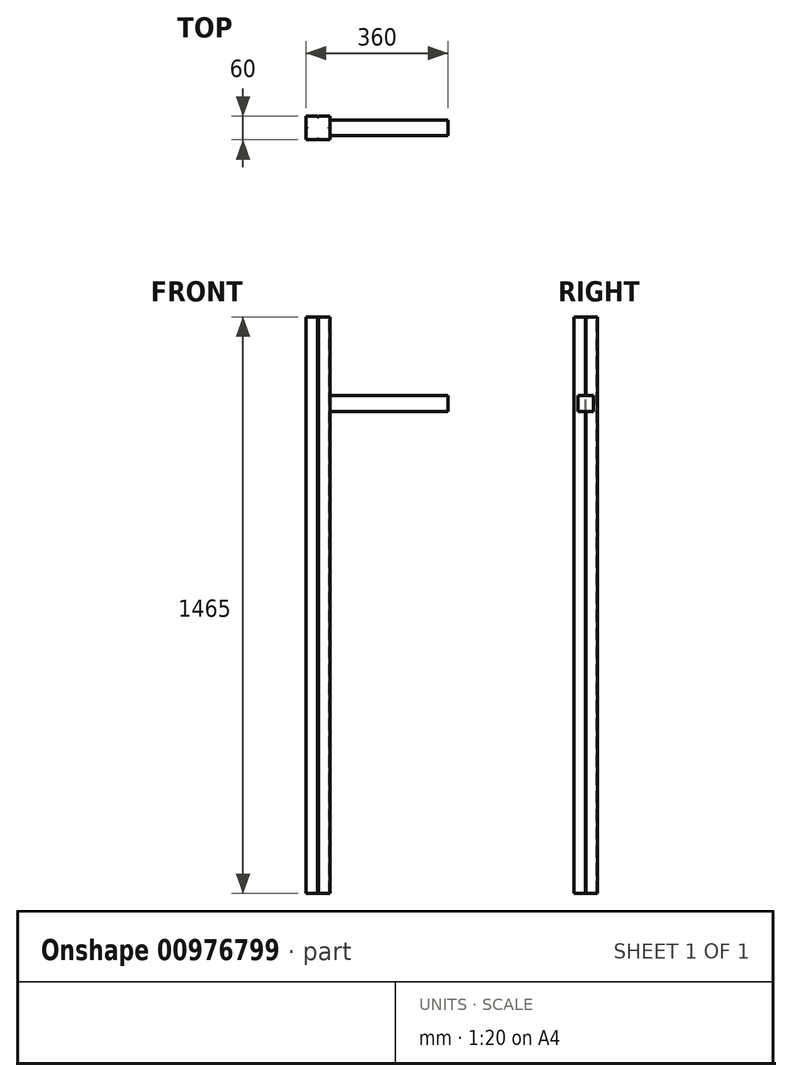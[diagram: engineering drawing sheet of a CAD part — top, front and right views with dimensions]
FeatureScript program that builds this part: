
annotation { "Feature Type Name" : "Feature", "Feature Type Description" : "" }
export const myFeature = defineFeature(function(context is Context, id is Id, definition is map)
    precondition{}
    {
        {
            var Q0;
            Q0=qCreatedBy(makeId("Top.planeOp"),FACE);
            var sketch = newSketch(context, id + "F0", { "sketchPlane" : qUnion([Q0])});
            skLineSegment(sketch, "E0.bottom", {"start": v(30, -30) * mm, "end": v(-30, -30) * mm});
            skLineSegment(sketch, "E0.top", {"start": v(30, 30) * mm, "end": v(-30, 30) * mm});
            skLineSegment(sketch, "E0.left", {"start": v(30, -30) * mm, "end": v(30, 30) * mm});
            skLineSegment(sketch, "E0.right", {"start": v(-30, -30) * mm, "end": v(-30, 30) * mm});
            skPoint(sketch, "E0.middle", {"position": v(0, 0) * mm});
            skSolve(sketch);
        }
        {
            var Q0;
            Q0 = qSketchRegion(id + "F0", true);
            extrude(context, id + "F1", {"entities" : qUnion([Q0]), "depth" : 1465 * mm, "offsetDistance" : 25.4 * mm});
        }
        {
            var Q0;
            Q0=makeQuery(id+"F1.opExtrude","CAP_FACE",FACE,{"disambiguationData":[OSD([sQuery(id+"F0.wireOp",EDGE,"E0.bottom"),sQuery(id+"F0.wireOp",EDGE,"E0.top"),sQuery(id+"F0.wireOp",EDGE,"E0.left"),sQuery(id+"F0.wireOp",EDGE,"E0.right")])],"isStart":false});
            var sketch = newSketch(context, id + "F2", { "sketchPlane" : qUnion([Q0])});
            skLineSegment(sketch, "E1", {"start": v(0, 45.9) * mm, "end": v(0, -43.6) * mm, "construction": true});
            skLineSegment(sketch, "E2", {"start": v(-50.22, 0) * mm, "end": v(51.37, 0) * mm, "construction": true});
            skLineSegment(sketch, "E3.bottom", {"start": v(-1, 30) * mm, "end": v(1, 30) * mm});
            skLineSegment(sketch, "E3.top", {"start": v(-1, 28) * mm, "end": v(1, 28) * mm});
            skLineSegment(sketch, "E3.left", {"start": v(-1, 30) * mm, "end": v(-1, 28) * mm});
            skLineSegment(sketch, "E3.right", {"start": v(1, 30) * mm, "end": v(1, 28) * mm});
            skLineSegment(sketch, "E4.bottom", {"start": v(-30, 1) * mm, "end": v(-28, 1) * mm});
            skLineSegment(sketch, "E4.top", {"start": v(-30, -1) * mm, "end": v(-28, -1) * mm});
            skLineSegment(sketch, "E4.left", {"start": v(-30, 1) * mm, "end": v(-30, -1) * mm});
            skLineSegment(sketch, "E4.right", {"start": v(-28, 1) * mm, "end": v(-28, -1) * mm});
            skLineSegment(sketch, "E5.bottom", {"start": v(-1, -30) * mm, "end": v(1, -30) * mm});
            skLineSegment(sketch, "E5.top", {"start": v(-1, -28) * mm, "end": v(1, -28) * mm});
            skLineSegment(sketch, "E5.left", {"start": v(-1, -30) * mm, "end": v(-1, -28) * mm});
            skLineSegment(sketch, "E5.right", {"start": v(1, -30) * mm, "end": v(1, -28) * mm});
            skLineSegment(sketch, "E6.bottom", {"start": v(30, 1) * mm, "end": v(28, 1) * mm});
            skLineSegment(sketch, "E6.top", {"start": v(30, -1) * mm, "end": v(28, -1) * mm});
            skLineSegment(sketch, "E6.left", {"start": v(30, 1) * mm, "end": v(30, -1) * mm});
            skLineSegment(sketch, "E6.right", {"start": v(28, 1) * mm, "end": v(28, -1) * mm});
            skSolve(sketch);
        }
        {
            var Q0;
            Q0 = qSketchRegion(id + "F2", true);
            extrude(context, id + "F3", {"entities" : qUnion([Q0]), "operationType" : NewBodyOperationType.REMOVE, "endBound" : BoundingType.UP_TO_NEXT, "oppositeDirection" : true, "depth" : 25.4 * mm, "offsetDistance" : 25.4 * mm});
        }
        {
            var Q0;
            {var subQ0=sQuery(id+"F0.wireOp",EDGE,"E0.bottom");var subQ2=sQuery(id+"F0.wireOp",EDGE,"E0.left");Q0=makeQuery(id+"F3.boolean.opBoolean","SPLIT",FACE,{"disambiguationData":[TD([makeQuery(id+"F1.opExtrude","SWEPT_FACE",FACE,{"disambiguationData":[OSD([subQ0])]})])],"derivedFrom":makeQuery(id+"F1.opExtrude","SWEPT_FACE",FACE,{"disambiguationData":[OSD([subQ2])]})});}
            var sketch = newSketch(context, id + "F4", { "sketchPlane" : qUnion([Q0])});
            skLineSegment(sketch, "E7.bottom", {"start": v(-20, 1265) * mm, "end": v(20, 1265) * mm});
            skLineSegment(sketch, "E7.top", {"start": v(-20, 1225) * mm, "end": v(20, 1225) * mm});
            skLineSegment(sketch, "E7.left", {"start": v(-20, 1265) * mm, "end": v(-20, 1225) * mm});
            skLineSegment(sketch, "E7.right", {"start": v(20, 1265) * mm, "end": v(20, 1225) * mm});
            skSolve(sketch);
        }
        {
            var Q0;
            Q0 = qSketchRegion(id + "F4", true);
            extrude(context, id + "F5", {"entities" : qUnion([Q0]), "operationType" : NewBodyOperationType.ADD, "depth" : 300 * mm, "offsetDistance" : 25.4 * mm});
        }
    });
